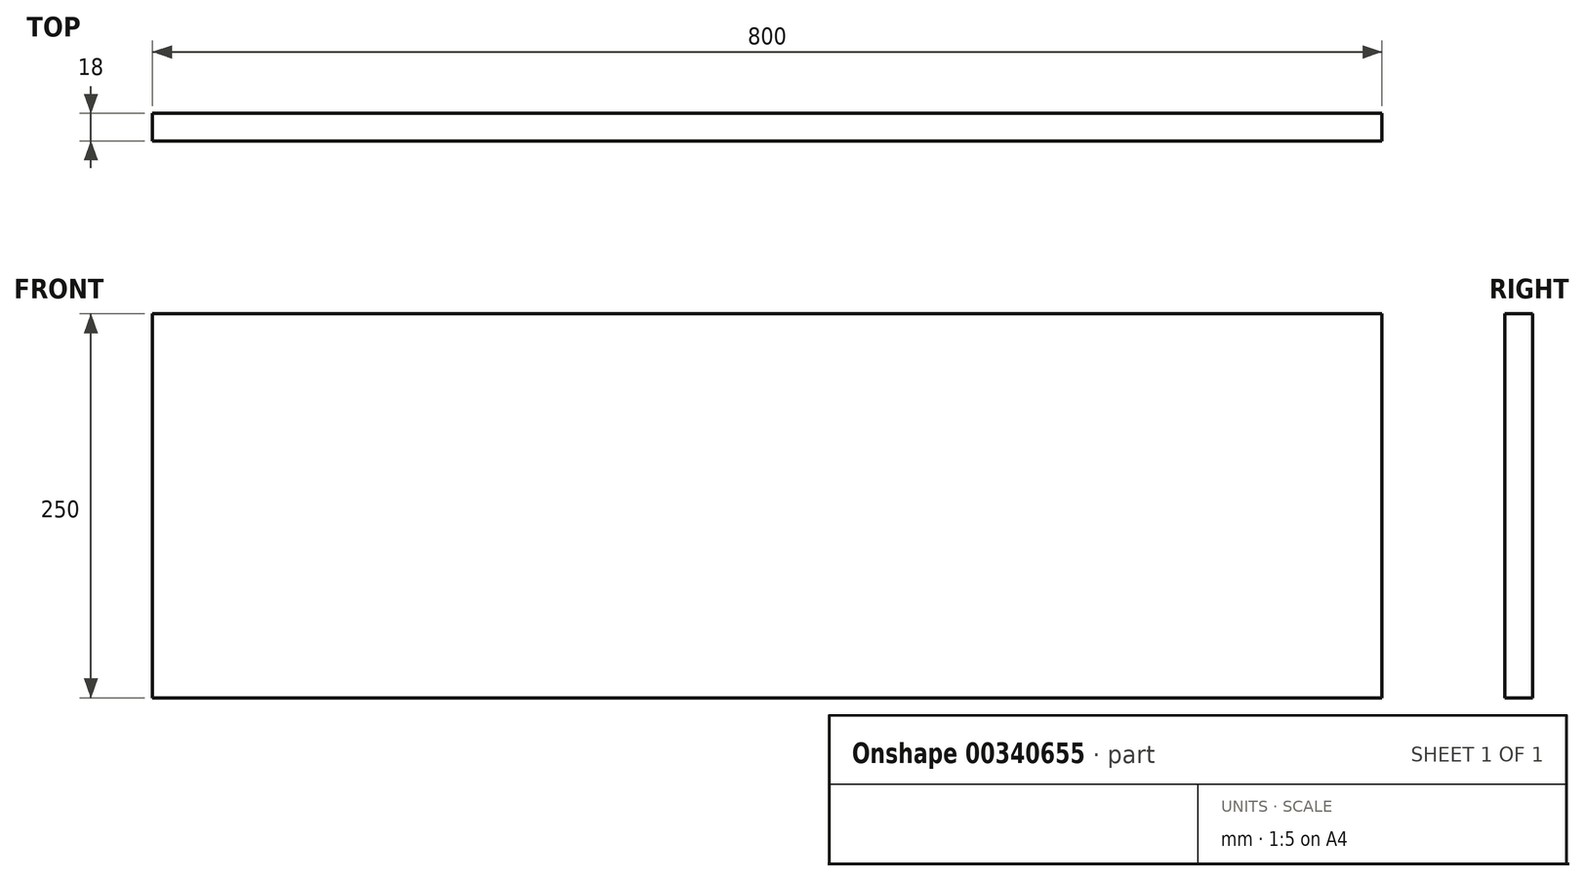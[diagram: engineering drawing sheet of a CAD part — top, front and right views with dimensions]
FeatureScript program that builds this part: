
annotation { "Feature Type Name" : "Feature", "Feature Type Description" : "" }
export const myFeature = defineFeature(function(context is Context, id is Id, definition is map)
    precondition{}
    {
        {
            var Q0;
            Q0=qCreatedBy(makeId("Front.planeOp"),FACE);
            var sketch = newSketch(context, id + "F0", { "sketchPlane" : qUnion([Q0])});
            skLineSegment(sketch, "E0.bottom", {"start": v(-401.6, -39.97) * mm, "end": v(398.4, -39.97) * mm});
            skLineSegment(sketch, "E0.top", {"start": v(-401.6, -289.97) * mm, "end": v(398.4, -289.97) * mm});
            skLineSegment(sketch, "E0.left", {"start": v(-401.6, -39.97) * mm, "end": v(-401.6, -289.97) * mm});
            skLineSegment(sketch, "E0.right", {"start": v(398.4, -39.97) * mm, "end": v(398.4, -289.97) * mm});
            skSolve(sketch);
        }
        {
            var Q0;
            Q0=makeQuery(id+"F0.imprint","IMPRINT",FACE,{"disambiguationData":[TD([[makeQuery(id+"F0.imprint","IMPRINT",EDGE,{"derivedFrom":sQuery(id+"F0.wireOp",EDGE,"E0.bottom")}),-1.0]])]});
            extrude(context, id + "F1", {"entities" : qUnion([Q0]), "depth" : 18 * mm});
        }
    });
